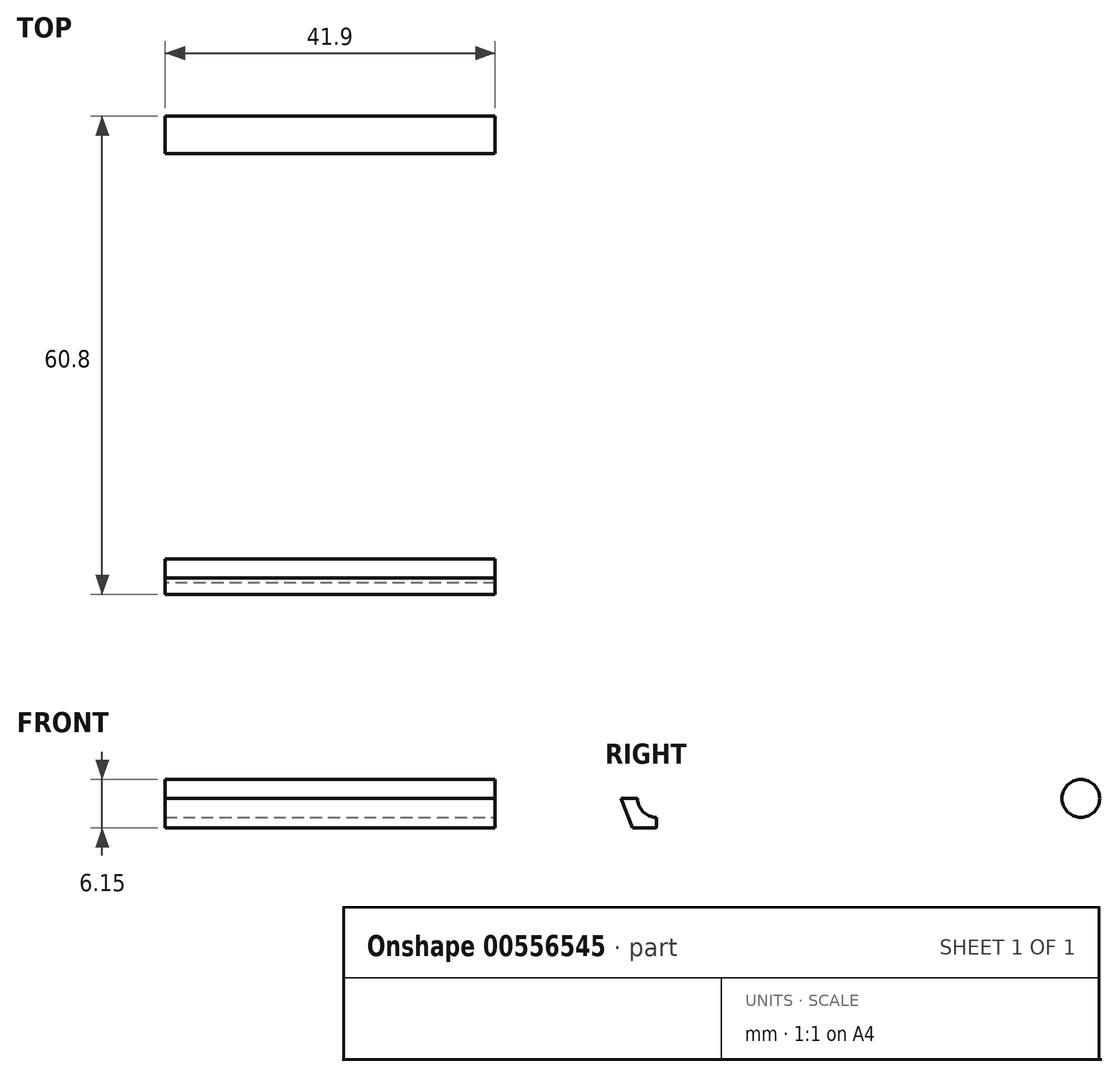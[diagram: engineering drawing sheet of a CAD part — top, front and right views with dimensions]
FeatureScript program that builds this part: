
annotation { "Feature Type Name" : "Feature", "Feature Type Description" : "" }
export const myFeature = defineFeature(function(context is Context, id is Id, definition is map)
    precondition{}
    {
        {
            var Q0;
            Q0=qCreatedBy(makeId("Top.planeOp"),FACE);
            var sketch = newSketch(context, id + "F0", { "sketchPlane" : qUnion([Q0])});
            skLineSegment(sketch, "E0.bottom", {"start": v(-20.95, 30) * mm, "end": v(20.95, 30) * mm});
            skLineSegment(sketch, "E0.top", {"start": v(-20.95, -30) * mm, "end": v(20.95, -30) * mm});
            skLineSegment(sketch, "E0.left", {"start": v(-20.95, 30) * mm, "end": v(-20.95, -30) * mm});
            skLineSegment(sketch, "E0.right", {"start": v(20.95, 30) * mm, "end": v(20.95, -30) * mm});
            skPoint(sketch, "E0.middle", {"position": v(0, 0) * mm});
            skSolve(sketch);
        }
        {
            var Q0;
            Q0=qCreatedBy(makeId("Right.planeOp"),FACE);
            var sketch = newSketch(context, id + "F1", { "sketchPlane" : qUnion([Q0])});
            skLineSegment(sketch, "E1.0", {"start": v(30, 0) * mm, "end": v(-30, 0) * mm});
            skLineSegment(sketch, "E2", {"start": v(-30, 38.75) * mm, "end": v(-45, 38.75) * mm});
            skLineSegment(sketch, "E3", {"start": v(-30, 38.75) * mm, "end": v(30, 38.75) * mm});
            skLineSegment(sketch, "E4", {"start": v(30, 38.75) * mm, "end": v(45, 38.75) * mm});
            skLineSegment(sketch, "E5", {"start": v(45, 38.75) * mm, "end": v(30, 0) * mm});
            skLineSegment(sketch, "E6", {"start": v(-45, 38.75) * mm, "end": v(-30, 0) * mm});
            skLineSegment(sketch, "E7", {"start": v(30, 38.75) * mm, "end": v(30, 0) * mm});
            skLineSegment(sketch, "E8", {"start": v(-30, 38.75) * mm, "end": v(-30, 0) * mm});
            skSolve(sketch);
        }
        {
            var Q0;
            Q0=makeQuery(id+"F1.imprint","IMPRINT",FACE,{"disambiguationData":[TD([[makeQuery(id+"F1.imprint","IMPRINT",EDGE,{"derivedFrom":sQuery(id+"F1.wireOp",EDGE,"E1.0")}),-1.0]])]});
            var Q1;
            Q1=makeQuery(id+"F1.imprint","IMPRINT",FACE,{"disambiguationData":[TD([[makeQuery(id+"F1.imprint","IMPRINT",EDGE,{"derivedFrom":sQuery(id+"F1.wireOp",EDGE,"E2")}),1.0]])]});
            var Q2;
            Q2=makeQuery(id+"F1.imprint","IMPRINT",FACE,{"disambiguationData":[TD([[makeQuery(id+"F1.imprint","IMPRINT",EDGE,{"derivedFrom":sQuery(id+"F1.wireOp",EDGE,"E4")}),-1.0]])]});
            extrude(context, id + "F2", {"entities" : qUnion([Q0, Q1, Q2]), "depth" : 20.95 * mm, "offsetDistance" : 25 * mm, "hasSecondDirection" : true, "secondDirectionOppositeDirection" : true, "secondDirectionDepth" : 20.95 * mm});
        }
        {
            var Q0;
            Q0=qCreatedBy(makeId("Front.planeOp"),FACE);
            var sketch = newSketch(context, id + "F3", { "sketchPlane" : qUnion([Q0])});
            skLineSegment(sketch, "E9.0", {"start": v(17.2, 35) * mm, "end": v(-17.2, 35) * mm});
            skLineSegment(sketch, "E9.1", {"start": v(17.2, 35) * mm, "end": v(17.2, 3.75) * mm});
            skLineSegment(sketch, "E9.2", {"start": v(-17.2, 3.75) * mm, "end": v(17.2, 3.75) * mm});
            skLineSegment(sketch, "E9.3", {"start": v(-17.2, 35) * mm, "end": v(-17.2, 3.75) * mm});
            skSolve(sketch);
        }
        {
            var Q0;
            Q0 = qSketchRegion(id + "F3", true);
            extrude(context, id + "F4", {"entities" : qUnion([Q0]), "operationType" : NewBodyOperationType.REMOVE, "endBound" : BoundingType.THROUGH_ALL, "oppositeDirection" : true, "depth" : 25 * mm, "offsetDistance" : 25 * mm, "hasSecondDirection" : true, "secondDirectionBound" : SecondDirectionBoundingType.THROUGH_ALL, "secondDirectionOppositeDirection" : false, "secondDirectionDepth" : 25 * mm});
        }
        {
            var Q0;
            Q0=makeQuery(id+"F4.boolean.opBoolean","COPY",FACE,{"derivedFrom":makeQuery(id+"F4.opExtrude","SWEPT_FACE",FACE,{"disambiguationData":[OSD([sQuery(id+"F3.wireOp",EDGE,"E9.2")])]})});
            var sketch = newSketch(context, id + "F5", { "sketchPlane" : qUnion([Q0])});
            skLineSegment(sketch, "E10", {"start": v(-17.2, -31.45) * mm, "end": v(-17.2, -27.45) * mm});
            skLineSegment(sketch, "E11", {"start": v(-17.2, -27.45) * mm, "end": v(-17.2, -22.45) * mm});
            skLineSegment(sketch, "E12", {"start": v(-17.2, -22.45) * mm, "end": v(17.2, -22.45) * mm});
            skLineSegment(sketch, "E13", {"start": v(17.2, -22.45) * mm, "end": v(17.2, -27.45) * mm});
            skLineSegment(sketch, "E14", {"start": v(17.2, -27.45) * mm, "end": v(17.2, -31.45) * mm});
            skLineSegment(sketch, "E15", {"start": v(17.2, -31.45) * mm, "end": v(-17.2, -31.45) * mm});
            skLineSegment(sketch, "E16.MirrorCS", {"start": v(-17.2, 22.45) * mm, "end": v(17.2, 22.45) * mm});
            skLineSegment(sketch, "E17.MirrorCS", {"start": v(17.2, 31.45) * mm, "end": v(-17.2, 31.45) * mm});
            skLineSegment(sketch, "E18.MirrorCS", {"start": v(17.2, 27.45) * mm, "end": v(17.2, 31.45) * mm});
            skLineSegment(sketch, "E19.MirrorCS", {"start": v(17.2, 22.45) * mm, "end": v(17.2, 27.45) * mm});
            skLineSegment(sketch, "E20.MirrorCS", {"start": v(-17.2, 27.45) * mm, "end": v(-17.2, 22.45) * mm});
            skLineSegment(sketch, "E21.MirrorCS", {"start": v(-17.2, 31.45) * mm, "end": v(-17.2, 27.45) * mm});
            skLineSegment(sketch, "E22", {"start": v(-17.2, -27.45) * mm, "end": v(17.2, -27.45) * mm});
            skLineSegment(sketch, "E23", {"start": v(-17.2, 27.45) * mm, "end": v(17.2, 27.45) * mm});
            skLineSegment(sketch, "E24.0", {"start": v(0, 30) * mm, "end": v(0, -30) * mm});
            skLineSegment(sketch, "E25", {"start": v(0, 31.45) * mm, "end": v(0, 10.45) * mm});
            skLineSegment(sketch, "E26", {"start": v(0, 31.45) * mm, "end": v(0, -8.55) * mm});
            skCircle(sketch, "E27.cCircle", {"center": v(0, 10.45) * mm, "radius": 5 * mm, "construction": true});
            skLineSegment(sketch, "E27.0", {"start": v(2.89, 5.45) * mm, "end": v(-2.89, 5.45) * mm});
            skLineSegment(sketch, "E27.1", {"start": v(-2.89, 5.45) * mm, "end": v(-5.77, 10.45) * mm});
            skLineSegment(sketch, "E27.2", {"start": v(-5.77, 10.45) * mm, "end": v(-2.89, 15.45) * mm});
            skLineSegment(sketch, "E27.3", {"start": v(-2.89, 15.45) * mm, "end": v(2.89, 15.45) * mm});
            skLineSegment(sketch, "E27.4", {"start": v(2.89, 15.45) * mm, "end": v(5.77, 10.45) * mm});
            skLineSegment(sketch, "E27.5", {"start": v(5.77, 10.45) * mm, "end": v(2.89, 5.45) * mm});
            skPoint(sketch, "E27.0.midPoint", {"position": v(0, 5.45) * mm});
            skCircle(sketch, "E28.cCircle", {"center": v(0, -8.55) * mm, "radius": 5 * mm, "construction": true});
            skLineSegment(sketch, "E28.0", {"start": v(2.89, -13.55) * mm, "end": v(-2.89, -13.55) * mm});
            skLineSegment(sketch, "E28.1", {"start": v(-2.89, -13.55) * mm, "end": v(-5.77, -8.55) * mm});
            skLineSegment(sketch, "E28.2", {"start": v(-5.77, -8.55) * mm, "end": v(-2.89, -3.55) * mm});
            skLineSegment(sketch, "E28.3", {"start": v(-2.89, -3.55) * mm, "end": v(2.89, -3.55) * mm});
            skLineSegment(sketch, "E28.4", {"start": v(2.89, -3.55) * mm, "end": v(5.77, -8.55) * mm});
            skLineSegment(sketch, "E28.5", {"start": v(5.77, -8.55) * mm, "end": v(2.89, -13.55) * mm});
            skPoint(sketch, "E28.0.midPoint", {"position": v(0, -13.55) * mm});
            skCircle(sketch, "E29", {"center": v(0, -8.55) * mm, "radius": 2.5 * mm});
            skCircle(sketch, "E30", {"center": v(0, 10.45) * mm, "radius": 2.5 * mm});
            skSolve(sketch);
        }
        {
            var Q0;
            Q0=makeQuery(id+"F5.imprint","IMPRINT",FACE,{"disambiguationData":[TD([[makeQuery(id+"F5.imprint","IMPRINT",EDGE,{"derivedFrom":sQuery(id+"F5.wireOp",EDGE,"E17.MirrorCS")}),1.0]])]});
            var Q1;
            Q1=makeQuery(id+"F5.imprint","IMPRINT",FACE,{"disambiguationData":[TD([[makeQuery(id+"F5.imprint","IMPRINT",EDGE,{"derivedFrom":sQuery(id+"F5.wireOp",EDGE,"E16.MirrorCS")}),1.0]])]});
            var Q2;
            Q2=makeQuery(id+"F5.imprint","IMPRINT",FACE,{"disambiguationData":[TD([[makeQuery(id+"F5.imprint","IMPRINT",EDGE,{"derivedFrom":sQuery(id+"F5.wireOp",EDGE,"E11")}),1.0]])]});
            var Q3;
            Q3=makeQuery(id+"F5.imprint","IMPRINT",FACE,{"disambiguationData":[TD([[makeQuery(id+"F5.imprint","IMPRINT",EDGE,{"derivedFrom":sQuery(id+"F5.wireOp",EDGE,"E10")}),1.0]])]});
            extrude(context, id + "F6", {"entities" : qUnion([Q0, Q1, Q2, Q3]), "operationType" : NewBodyOperationType.ADD, "depth" : 3.5 * mm, "offsetDistance" : 25 * mm});
        }
        {
            var Q0;
            Q0=makeQuery(id+"F6.opExtrude","CAP_EDGE",EDGE,{"disambiguationData":[OSD([sQuery(id+"F5.wireOp",EDGE,"E15")])],"isStart":false});
            var Q1;
            Q1=makeQuery(id+"F6.opExtrude","CAP_EDGE",EDGE,{"disambiguationData":[OSD([sQuery(id+"F5.wireOp",EDGE,"E17.MirrorCS")])],"isStart":false});
            fillet(context, id + "F7", {"entities" : qUnion([Q0, Q1]), "radius" : 4 * mm, "tangentPropagation" : true, "allowEdgeOverflow" : false});
        }
        {
            var Q0;
            Q0=makeQuery(id+"F6.opExtrude","CAP_EDGE",EDGE,{"disambiguationData":[OSD([sQuery(id+"F5.wireOp",EDGE,"E16.MirrorCS")])],"isStart":false});
            var Q1;
            Q1=makeQuery(id+"F6.opExtrude","CAP_EDGE",EDGE,{"disambiguationData":[OSD([sQuery(id+"F5.wireOp",EDGE,"E12")])],"isStart":false});
            fillet(context, id + "F8", {"entities" : qUnion([Q0, Q1]), "radius" : 5 * mm, "tangentPropagation" : true, "allowEdgeOverflow" : false});
        }
        {
            var Q0;
            Q0=qCreatedBy(makeId("Front.planeOp"),FACE);
            var sketch = newSketch(context, id + "F9", { "sketchPlane" : qUnion([Q0])});
            skLineSegment(sketch, "E31.0", {"start": v(-17.2, 35) * mm, "end": v(17.2, 35) * mm});
            skLineSegment(sketch, "E31.1", {"start": v(17.2, 3.75) * mm, "end": v(17.2, 26) * mm});
            skPoint(sketch, "E32.visualSharp", {"position": v(17.2, 35) * mm});
            skLineSegment(sketch, "E33", {"start": v(7.2, 35) * mm, "end": v(4.2, 35) * mm});
            skLineSegment(sketch, "E34", {"start": v(17.2, 26) * mm, "end": v(17.2, 22) * mm});
            skArc(sketch, "E35.filletArc", {"start": v(17.2, 22) * mm, "mid": v(13.4, 31.2) * mm, "end": v(4.2, 35) * mm});
            skArc(sketch, "E36.MirrorCS", {"start": v(-17.2, 22) * mm, "mid": v(-13.4, 31.2) * mm, "end": v(-4.2, 35) * mm});
            skLineSegment(sketch, "E37", {"start": v(17.2, 22) * mm, "end": v(17.2, 35) * mm});
            skLineSegment(sketch, "E38.MirrorCS", {"start": v(-17.2, 22) * mm, "end": v(-17.2, 35) * mm});
            skLineSegment(sketch, "E39.MirrorCS", {"start": v(17.2, 35) * mm, "end": v(-17.2, 35) * mm});
            skSolve(sketch);
        }
        {
            var Q0;
            Q0 = qSketchRegion(id + "F9", true);
            var Q1;
            Q1=makeQuery(id+"F2.opExtrude","SWEPT_FACE",FACE,{"disambiguationData":[OSD([sQuery(id+"F1.wireOp",EDGE,"E6")])]});
            var Q2;
            Q2=makeQuery(id+"F2.opExtrude","SWEPT_FACE",FACE,{"disambiguationData":[OSD([sQuery(id+"F1.wireOp",EDGE,"E5")])]});
            extrude(context, id + "F10", {"entities" : qUnion([Q0]), "operationType" : NewBodyOperationType.ADD, "endBound" : BoundingType.UP_TO_SURFACE, "depth" : 25 * mm, "endBoundEntityFace" : qUnion([Q1]), "offsetDistance" : 25 * mm, "hasSecondDirection" : true, "secondDirectionBound" : SecondDirectionBoundingType.UP_TO_SURFACE, "secondDirectionOppositeDirection" : true, "secondDirectionDepth" : 25 * mm, "secondDirectionBoundEntityFace" : qUnion([Q2])});
        }
        {
            var Q0;
            Q0=makeQuery(id+"F2.opExtrude","CAP_FACE",FACE,{"disambiguationData":[OSD([sQuery(id+"F1.wireOp",EDGE,"E1.0"),sQuery(id+"F1.wireOp",EDGE,"E2"),sQuery(id+"F1.wireOp",EDGE,"E3"),sQuery(id+"F1.wireOp",EDGE,"E4"),sQuery(id+"F1.wireOp",EDGE,"E5"),sQuery(id+"F1.wireOp",EDGE,"E6")])],"isStart":false});
            var sketch = newSketch(context, id + "F11", { "sketchPlane" : qUnion([Q0])});
            skLineSegment(sketch, "E40", {"start": v(-26.95, 0) * mm, "end": v(-26.95, 3.75) * mm});
            skLineSegment(sketch, "E41", {"start": v(-26.95, 3.75) * mm, "end": v(-31.45, 3.75) * mm});
            skCircle(sketch, "E42", {"center": v(-26.95, 3.75) * mm, "radius": 2.4 * mm});
            skCircle(sketch, "E43.MirrorC", {"center": v(26.95, 3.75) * mm, "radius": 2.4 * mm});
            skSolve(sketch);
        }
        {
            var Q0;
            {var subQ0=sQuery(id+"F11.wireOp",EDGE,"E41");var subQ1=sQuery(id+"F11.wireOp",EDGE,"E40");var subQ2=makeQuery(id+"F11.imprint","INTERSECT",VERTEX,{"derivedFrom":[subQ1,subQ0]});Q0=makeQuery(id+"F11.imprint","IMPRINT",FACE,{"disambiguationData":[TD([[makeQuery(id+"F11.imprint","IMPRINT",EDGE,{"disambiguationData":[TD([[subQ2,1.0]])],"derivedFrom":subQ1}),1.0]])]});}
            var Q1;
            {var subQ0=sQuery(id+"F11.wireOp",EDGE,"E41");var subQ1=sQuery(id+"F11.wireOp",EDGE,"E40");var subQ2=makeQuery(id+"F11.imprint","INTERSECT",VERTEX,{"derivedFrom":[subQ1,subQ0]});Q1=makeQuery(id+"F11.imprint","IMPRINT",FACE,{"disambiguationData":[TD([[makeQuery(id+"F11.imprint","IMPRINT",EDGE,{"disambiguationData":[TD([[subQ2,1.0]])],"derivedFrom":subQ1}),-1.0]])]});}
            var Q2;
            Q2=makeQuery(id+"F11.imprint","IMPRINT",FACE,{"disambiguationData":[TD([[makeQuery(id+"F11.imprint","IMPRINT",EDGE,{"derivedFrom":sQuery(id+"F11.wireOp",EDGE,"E43.MirrorC")}),-1.0]])]});
            extrude(context, id + "F12", {"entities" : qUnion([Q0, Q1, Q2]), "operationType" : NewBodyOperationType.REMOVE, "endBound" : BoundingType.THROUGH_ALL, "oppositeDirection" : true, "depth" : 25 * mm, "offsetDistance" : 25 * mm});
        }
        {
            var Q0;
            {var subQ0=sQuery(id+"F5.wireOp",EDGE,"E27.4");Q0=makeQuery(id+"F5.imprint","IMPRINT",FACE,{"disambiguationData":[TD([[makeQuery(id+"F5.imprint","IMPRINT",EDGE,{"derivedFrom":subQ0}),-1.0]])]});}
            var Q1;
            {var subQ0=sQuery(id+"F5.wireOp",EDGE,"E28.4");Q1=makeQuery(id+"F5.imprint","IMPRINT",FACE,{"disambiguationData":[TD([[makeQuery(id+"F5.imprint","IMPRINT",EDGE,{"derivedFrom":subQ0}),-1.0]])]});}
            var Q2;
            {var subQ0=sQuery(id+"F5.wireOp",EDGE,"E27.1");Q2=makeQuery(id+"F5.imprint","IMPRINT",FACE,{"disambiguationData":[TD([[makeQuery(id+"F5.imprint","IMPRINT",EDGE,{"derivedFrom":subQ0}),-1.0]])]});}
            var Q3;
            {var subQ0=sQuery(id+"F5.wireOp",EDGE,"E28.1");Q3=makeQuery(id+"F5.imprint","IMPRINT",FACE,{"disambiguationData":[TD([[makeQuery(id+"F5.imprint","IMPRINT",EDGE,{"derivedFrom":subQ0}),-1.0]])]});}
            extrude(context, id + "F13", {"entities" : qUnion([Q0, Q1, Q2, Q3]), "operationType" : NewBodyOperationType.REMOVE, "oppositeDirection" : true, "depth" : 3.1 * mm, "offsetDistance" : 25 * mm});
        }
        {
            var Q0;
            {var subQ0=sQuery(id+"F5.wireOp",EDGE,"E26");var subQ1=makeQuery(id+"F5.imprint","IMPRINT",VERTEX,{"disambiguationData":[OD(1.0)],"derivedFrom":subQ0});Q0=makeQuery(id+"F5.imprint","IMPRINT",FACE,{"disambiguationData":[TD([[makeQuery(id+"F5.imprint","IMPRINT",EDGE,{"disambiguationData":[TD([[subQ1,1.0]])],"derivedFrom":subQ0}),1.0]])]});}
            var Q1;
            {var subQ0=sQuery(id+"F5.wireOp",EDGE,"E26");var subQ1=sQuery(id+"F5.wireOp",EDGE,"E24.0");var subQ2=makeQuery(id+"F5.imprint","INTERSECT",VERTEX,{"derivedFrom":[subQ1,subQ0]});Q1=makeQuery(id+"F5.imprint","IMPRINT",FACE,{"disambiguationData":[TD([[makeQuery(id+"F5.imprint","IMPRINT",EDGE,{"disambiguationData":[TD([[subQ2,-1.0]])],"derivedFrom":subQ1}),1.0]])]});}
            var Q2;
            {var subQ0=sQuery(id+"F5.wireOp",EDGE,"E26");var subQ1=makeQuery(id+"F5.imprint","IMPRINT",VERTEX,{"disambiguationData":[OD(1.0)],"derivedFrom":subQ0});Q2=makeQuery(id+"F5.imprint","IMPRINT",FACE,{"disambiguationData":[TD([[makeQuery(id+"F5.imprint","IMPRINT",EDGE,{"disambiguationData":[TD([[subQ1,1.0]])],"derivedFrom":subQ0}),-1.0]])]});}
            var Q3;
            {var subQ0=sQuery(id+"F5.wireOp",EDGE,"E26");var subQ1=sQuery(id+"F5.wireOp",EDGE,"E24.0");var subQ2=makeQuery(id+"F5.imprint","INTERSECT",VERTEX,{"derivedFrom":[subQ1,subQ0]});Q3=makeQuery(id+"F5.imprint","IMPRINT",FACE,{"disambiguationData":[TD([[makeQuery(id+"F5.imprint","IMPRINT",EDGE,{"disambiguationData":[TD([[subQ2,-1.0]])],"derivedFrom":subQ1}),-1.0]])]});}
            extrude(context, id + "F14", {"entities" : qUnion([Q0, Q1, Q2, Q3]), "operationType" : NewBodyOperationType.REMOVE, "endBound" : BoundingType.THROUGH_ALL, "oppositeDirection" : true, "depth" : 25 * mm, "offsetDistance" : 25 * mm});
        }
    });
